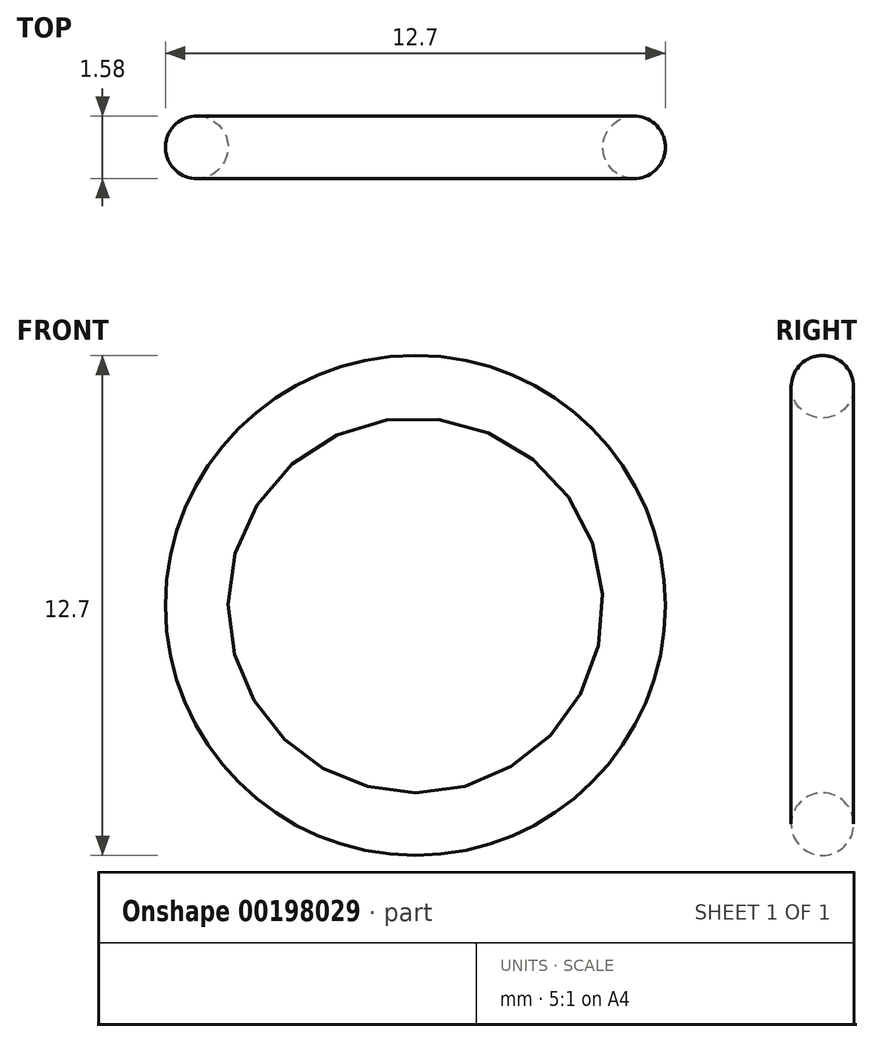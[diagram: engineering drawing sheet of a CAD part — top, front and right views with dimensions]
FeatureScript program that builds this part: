
annotation { "Feature Type Name" : "Feature", "Feature Type Description" : "" }
export const myFeature = defineFeature(function(context is Context, id is Id, definition is map)
    precondition{}
    {
        {
            var Q0;
            Q0=qCreatedBy(makeId("Front.planeOp"),FACE);
            var sketch = newSketch(context, id + "F0", { "sketchPlane" : qUnion([Q0])});
            skCircle(sketch, "E0", {"center": v(0, 0) * mm, "radius": 4.76 * mm});
            skSolve(sketch);
        }
        {
            var Q0;
            Q0=qCreatedBy(makeId("Right.planeOp"),FACE);
            var sketch = newSketch(context, id + "F1", { "sketchPlane" : qUnion([Q0])});
            skCircle(sketch, "E1", {"center": v(0, 5.56) * mm, "radius": 0.8 * mm});
            skSolve(sketch);
        }
        {
            var Q0;
            Q0=makeQuery(id+"F1.imprint","IMPRINT",FACE,{"disambiguationData":[TD([[makeQuery(id+"F1.imprint","IMPRINT",EDGE,{"derivedFrom":sQuery(id+"F1.wireOp",EDGE,"E1")}),1.0]])]});
            var Q1;
            Q1=sQuery(id+"F0.wireOp",EDGE,"E0");
            sweep(context, id + "F2", {"profiles" : qUnion([Q0]), "path" : qUnion([Q1])});
        }
    });
